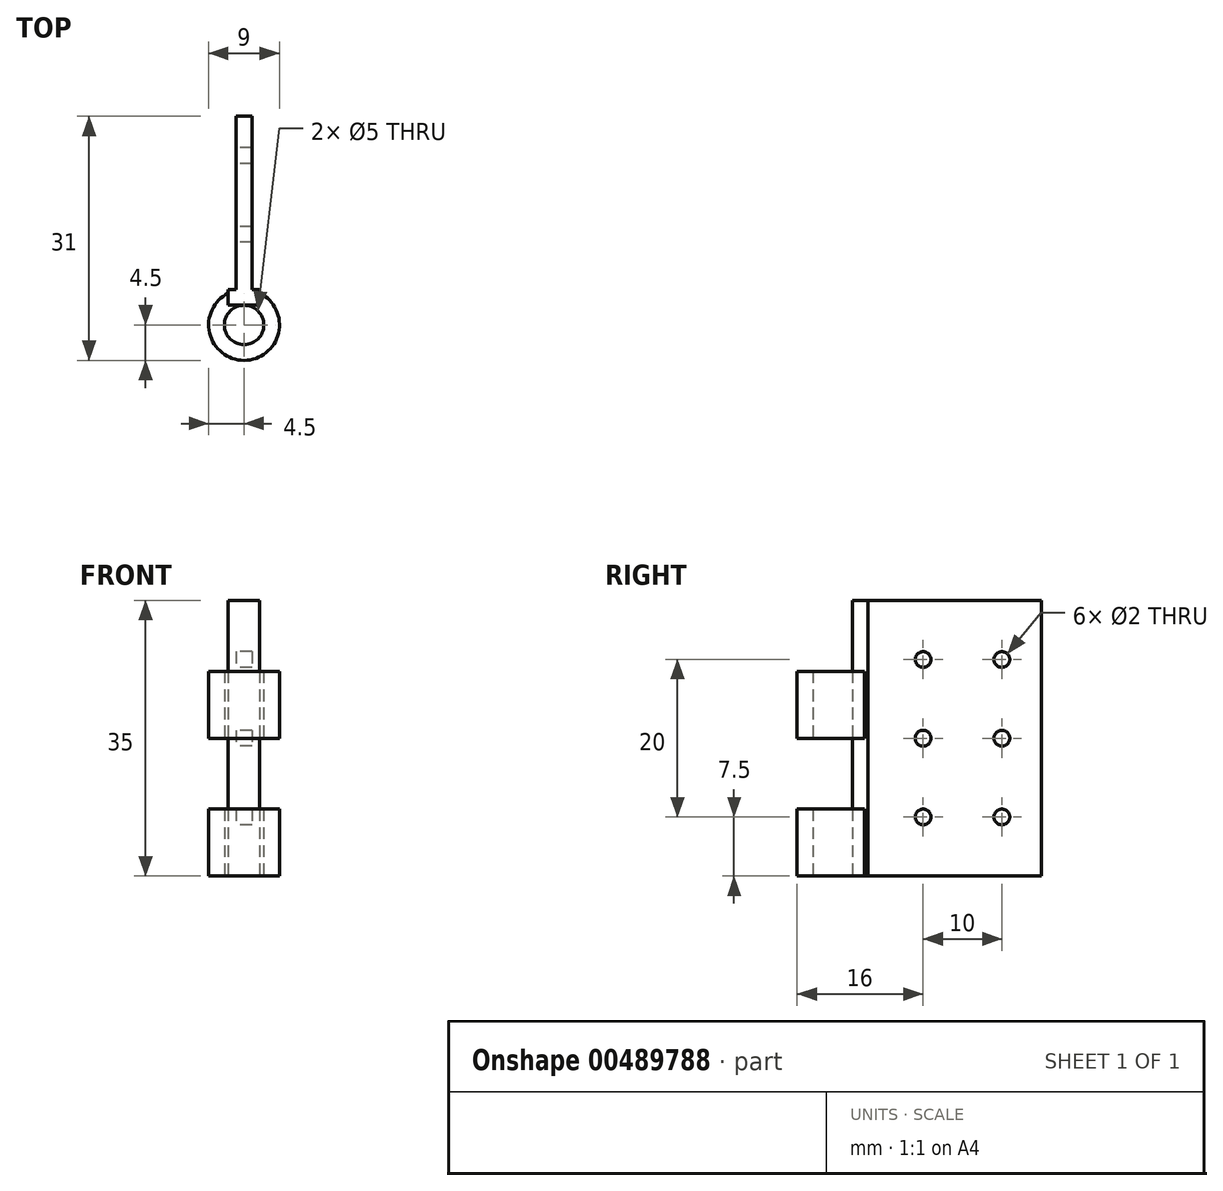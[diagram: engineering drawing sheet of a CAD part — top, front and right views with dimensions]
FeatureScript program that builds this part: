
annotation { "Feature Type Name" : "Feature", "Feature Type Description" : "" }
export const myFeature = defineFeature(function(context is Context, id is Id, definition is map)
    precondition{}
    {
        {
            var Q0;
            Q0=qCreatedBy(makeId("Front.planeOp"),FACE);
            var sketch = newSketch(context, id + "F0", { "sketchPlane" : qUnion([Q0])});
            skLineSegment(sketch, "E0.bottom", {"start": v(1, -17.5) * mm, "end": v(-1, -17.5) * mm});
            skLineSegment(sketch, "E0.top", {"start": v(1, 17.5) * mm, "end": v(-1, 17.5) * mm});
            skLineSegment(sketch, "E0.left", {"start": v(1, -17.5) * mm, "end": v(1, 17.5) * mm});
            skLineSegment(sketch, "E0.right", {"start": v(-1, -17.5) * mm, "end": v(-1, 17.5) * mm});
            skSolve(sketch);
        }
        {
            var Q0;
            Q0=makeQuery(id+"F0.imprint","IMPRINT",FACE,{"disambiguationData":[TD([[makeQuery(id+"F0.imprint","IMPRINT",EDGE,{"derivedFrom":sQuery(id+"F0.wireOp",EDGE,"E0.bottom")}),-1.0]])]});
            extrude(context, id + "F1", {"entities" : qUnion([Q0]), "depth" : 22 * mm});
        }
        {
            var Q0;
            Q0=makeQuery(id+"F1.opExtrude","SWEPT_FACE",FACE,{"disambiguationData":[OSD([sQuery(id+"F0.wireOp",EDGE,"E0.right")])]});
            var sketch = newSketch(context, id + "F2", { "sketchPlane" : qUnion([Q0])});
            skCircle(sketch, "E1", {"center": v(15, 10) * mm, "radius": 1 * mm});
            skCircle(sketch, "E2", {"center": v(5, 10) * mm, "radius": 1 * mm});
            skCircle(sketch, "E3", {"center": v(15, 0) * mm, "radius": 1 * mm});
            skCircle(sketch, "E4", {"center": v(5, 0) * mm, "radius": 1 * mm});
            skCircle(sketch, "E5", {"center": v(15, -10) * mm, "radius": 1 * mm});
            skCircle(sketch, "E6", {"center": v(5, -10) * mm, "radius": 1 * mm});
            skSolve(sketch);
        }
        {
            var Q0;
            Q0=makeQuery(id+"F2.imprint","IMPRINT",FACE,{"disambiguationData":[TD([[makeQuery(id+"F2.imprint","IMPRINT",EDGE,{"derivedFrom":sQuery(id+"F2.wireOp",EDGE,"E2")}),1.0]])]});
            var Q1;
            Q1=makeQuery(id+"F2.imprint","IMPRINT",FACE,{"disambiguationData":[TD([[makeQuery(id+"F2.imprint","IMPRINT",EDGE,{"derivedFrom":sQuery(id+"F2.wireOp",EDGE,"E1")}),1.0]])]});
            var Q2;
            Q2=makeQuery(id+"F2.imprint","IMPRINT",FACE,{"disambiguationData":[TD([[makeQuery(id+"F2.imprint","IMPRINT",EDGE,{"derivedFrom":sQuery(id+"F2.wireOp",EDGE,"E3")}),1.0]])]});
            var Q3;
            Q3=makeQuery(id+"F2.imprint","IMPRINT",FACE,{"disambiguationData":[TD([[makeQuery(id+"F2.imprint","IMPRINT",EDGE,{"derivedFrom":sQuery(id+"F2.wireOp",EDGE,"E4")}),1.0]])]});
            var Q4;
            Q4=makeQuery(id+"F2.imprint","IMPRINT",FACE,{"disambiguationData":[TD([[makeQuery(id+"F2.imprint","IMPRINT",EDGE,{"derivedFrom":sQuery(id+"F2.wireOp",EDGE,"E6")}),1.0]])]});
            var Q5;
            Q5=makeQuery(id+"F2.imprint","IMPRINT",FACE,{"disambiguationData":[TD([[makeQuery(id+"F2.imprint","IMPRINT",EDGE,{"derivedFrom":sQuery(id+"F2.wireOp",EDGE,"E5")}),1.0]])]});
            extrude(context, id + "F3", {"entities" : qUnion([Q0, Q1, Q2, Q3, Q4, Q5]), "operationType" : NewBodyOperationType.REMOVE, "oppositeDirection" : true, "depth" : 25 * mm});
        }
        {
            var Q0;
            Q0=makeQuery(id+"F1.opExtrude","CAP_FACE",FACE,{"disambiguationData":[OSD([sQuery(id+"F0.wireOp",EDGE,"E0.bottom"),sQuery(id+"F0.wireOp",EDGE,"E0.top"),sQuery(id+"F0.wireOp",EDGE,"E0.left"),sQuery(id+"F0.wireOp",EDGE,"E0.right")])],"isStart":false});
            var sketch = newSketch(context, id + "F4", { "sketchPlane" : qUnion([Q0])});
            skLineSegment(sketch, "E7.bottom", {"start": v(-2, 17.5) * mm, "end": v(2, 17.5) * mm});
            skLineSegment(sketch, "E7.top", {"start": v(-2, -17.5) * mm, "end": v(2, -17.5) * mm});
            skLineSegment(sketch, "E7.left", {"start": v(-2, 17.5) * mm, "end": v(-2, -17.5) * mm});
            skLineSegment(sketch, "E7.right", {"start": v(2, 17.5) * mm, "end": v(2, -17.5) * mm});
            skSolve(sketch);
        }
        {
            var Q0;
            {var subQ2=sQuery(id+"F4.wireOp",EDGE,"E7.left");Q0=makeQuery(id+"F4.imprint","IMPRINT",FACE,{"disambiguationData":[TD([[makeQuery(id+"F4.imprint","IMPRINT",EDGE,{"derivedFrom":subQ2}),1.0]])]});}
            var Q1;
            {var subQ2=sQuery(id+"F4.wireOp",EDGE,"E7.right");Q1=makeQuery(id+"F4.imprint","IMPRINT",FACE,{"disambiguationData":[TD([[makeQuery(id+"F4.imprint","IMPRINT",EDGE,{"derivedFrom":subQ2}),-1.0]])]});}
            var Q2;
            {var subQ1=makeQuery(id+"F1.opExtrude","CAP_EDGE",EDGE,{"disambiguationData":[OSD([sQuery(id+"F0.wireOp",EDGE,"E0.left")])],"isStart":false});Q2=makeQuery(id+"F4.imprint","IMPRINT",FACE,{"disambiguationData":[TD([[makeQuery(id+"F4.imprint","IMPRINT",EDGE,{"derivedFrom":subQ1}),1.0]])]});}
            extrude(context, id + "F5", {"entities" : qUnion([Q0, Q1, Q2]), "operationType" : NewBodyOperationType.ADD, "depth" : 2 * mm});
        }
        {
            var Q0;
            Q0=makeQuery(id+"F5.boolean.opBoolean","MERGE",FACE,{"derivedFrom":[makeQuery(id+"F1.opExtrude","SWEPT_FACE",FACE,{"disambiguationData":[OSD([sQuery(id+"F0.wireOp",EDGE,"E0.bottom")])]}),makeQuery(id+"F5.opExtrude","SWEPT_FACE",FACE,{"disambiguationData":[OSD([sQuery(id+"F4.wireOp",EDGE,"E7.top")])]})]});
            var sketch = newSketch(context, id + "F6", { "sketchPlane" : qUnion([Q0])});
            skCircle(sketch, "E8", {"center": v(0, 26.5) * mm, "radius": 2.5 * mm});
            skPoint(sketch, "E8.centerSnap0", {"position": v(0, 24) * mm});
            skCircle(sketch, "E9", {"center": v(0, 26.5) * mm, "radius": 4.5 * mm});
            skSolve(sketch);
        }
        {
            var Q0;
            {var subQ0=sQuery(id+"F0.wireOp",EDGE,"E0.bottom");Q0=makeQuery(id+"F6.imprint","IMPRINT",FACE,{"disambiguationData":[TD([[makeQuery(id+"F6.imprint","IMPRINT",EDGE,{"derivedFrom":makeQuery(id+"F1.opExtrude","CAP_EDGE",EDGE,{"disambiguationData":[OSD([subQ0])],"isStart":true})}),-1.0]])]});}
            cPlane(context, id + "F7", {"entities" : qUnion([Q0]), "cplaneType" : CPlaneType.OFFSET, "offset" : 17.5 * mm, "oppositeDirection" : true, "width" : 150 * mm, "height" : 150 * mm});
        }
        {
            var Q0;
            Q0=qCreatedBy(id+"F7.planeOp",FACE);
            var sketch = newSketch(context, id + "F8", { "sketchPlane" : qUnion([Q0])});
            skCircle(sketch, "E10", {"center": v(0, 26.5) * mm, "radius": 2.5 * mm});
            skCircle(sketch, "E11", {"center": v(0, 26.5) * mm, "radius": 4.5 * mm});
            skSolve(sketch);
        }
        {
            var Q0;
            Q0=makeQuery(id+"F8.imprint","IMPRINT",FACE,{"disambiguationData":[TD([[makeQuery(id+"F8.imprint","IMPRINT",EDGE,{"derivedFrom":sQuery(id+"F8.wireOp",EDGE,"E10")}),-1.0]])]});
            var Q1;
            {var subQ0=sQuery(id+"F6.wireOp",EDGE,"E8");Q1=makeQuery(id+"F6.imprint","IMPRINT",FACE,{"disambiguationData":[TD([[makeQuery(id+"F6.imprint","IMPRINT",EDGE,{"derivedFrom":subQ0}),-1.0]])]});}
            var Q2;
            {var subQ0=sQuery(id+"F6.wireOp",EDGE,"E9");var subQ1=makeQuery(id+"F5.opExtrude","CAP_EDGE",EDGE,{"disambiguationData":[OSD([sQuery(id+"F4.wireOp",EDGE,"E7.top")])],"isStart":false});var subQ2=makeQuery(id+"F6.imprint","INTERSECT",VERTEX,{"disambiguationData":[OD(0.0)],"derivedFrom":[subQ1,subQ0]});Q2=makeQuery(id+"F6.imprint","IMPRINT",FACE,{"disambiguationData":[TD([[makeQuery(id+"F6.imprint","IMPRINT",EDGE,{"disambiguationData":[TD([[subQ2,-1.0]])],"derivedFrom":subQ0}),1.0]])]});}
            extrude(context, id + "F9", {"entities" : qUnion([Q0, Q1, Q2]), "operationType" : NewBodyOperationType.ADD, "oppositeDirection" : true, "depth" : 8.5 * mm});
        }
    });
